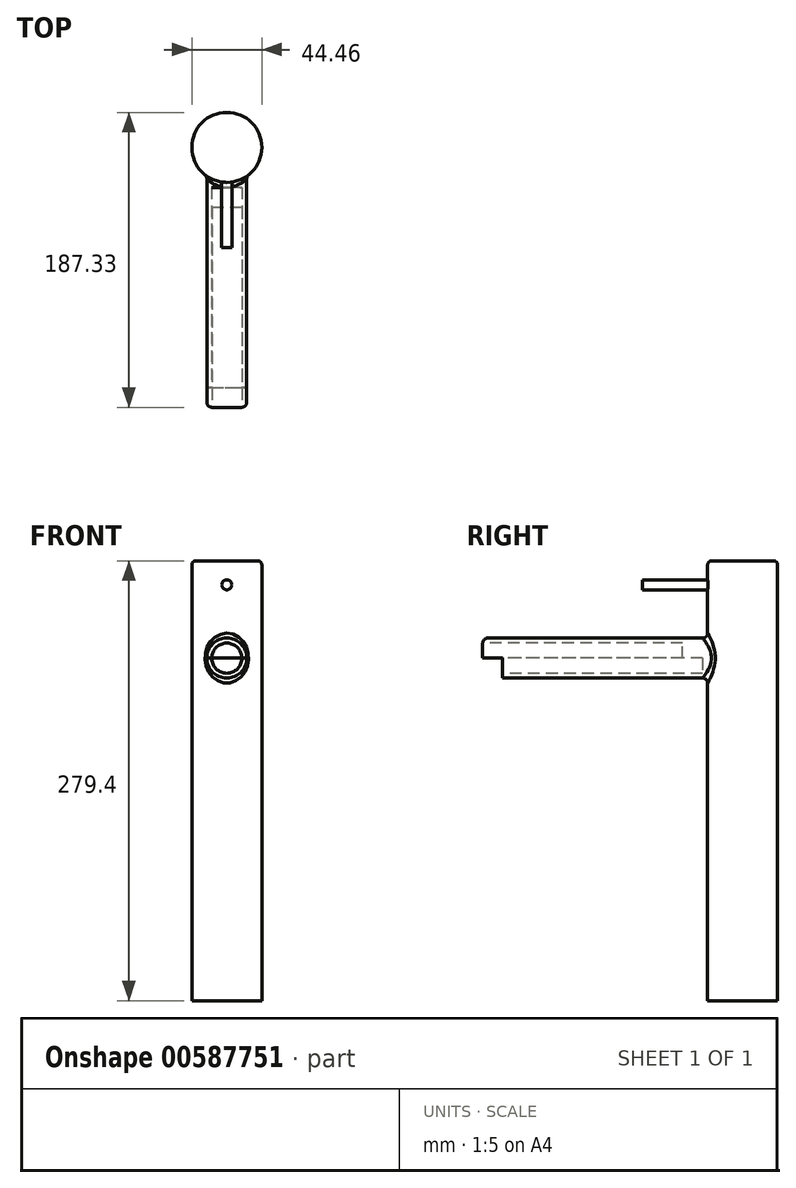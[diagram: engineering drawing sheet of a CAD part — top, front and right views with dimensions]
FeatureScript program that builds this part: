
annotation { "Feature Type Name" : "Feature", "Feature Type Description" : "" }
export const myFeature = defineFeature(function(context is Context, id is Id, definition is map)
    precondition{}
    {
        {
            var Q0;
            Q0=qCreatedBy(makeId("Top.planeOp"),FACE);
            var sketch = newSketch(context, id + "F0", { "sketchPlane" : qUnion([Q0])});
            skCircle(sketch, "E0", {"center": v(0, 0) * mm, "radius": 22.23 * mm});
            skSolve(sketch);
        }
        {
            var Q0;
            Q0=makeQuery(id+"F0.imprint","IMPRINT",FACE,{"disambiguationData":[TD([[makeQuery(id+"F0.imprint","IMPRINT",EDGE,{"derivedFrom":sQuery(id+"F0.wireOp",EDGE,"E0")}),1.0]])]});
            extrude(context, id + "F1", {"entities" : qUnion([Q0]), "depth" : 279.4 * mm, "offsetDistance" : 25.4 * mm});
        }
        {
            var Q0;
            Q0=makeQuery(id+"F1.opExtrude","CAP_EDGE",EDGE,{"disambiguationData":[OSD([sQuery(id+"F0.wireOp",EDGE,"E0")])],"isStart":false});
            fillet(context, id + "F2", {"entities" : qUnion([Q0]), "radius" : 2.54 * mm, "tangentPropagation" : true, "allowEdgeOverflow" : false});
        }
        {
            var Q0;
            Q0=qCreatedBy(makeId("Front.planeOp"),FACE);
            var sketch = newSketch(context, id + "F3", { "sketchPlane" : qUnion([Q0])});
            skCircle(sketch, "E1", {"center": v(0, 217.6) * mm, "radius": 12.7 * mm});
            skSolve(sketch);
        }
        {
            var Q0;
            Q0 = qSketchRegion(id + "F3", true);
            extrude(context, id + "F4", {"entities" : qUnion([Q0]), "operationType" : NewBodyOperationType.ADD, "depth" : 152.4 * mm, "offsetDistance" : 25.4 * mm});
        }
        {
            var Q0;
            Q0=makeQuery(id+"F4.boolean.opBoolean","INTERSECT",EDGE,{"derivedFrom":[makeQuery(id+"F1.opExtrude","SWEPT_FACE",FACE,{"disambiguationData":[OSD([sQuery(id+"F0.wireOp",EDGE,"E0")])]}),makeQuery(id+"F4.opExtrude","SWEPT_FACE",FACE,{"disambiguationData":[OSD([sQuery(id+"F3.wireOp",EDGE,"E1")])]})]});
            fillet(context, id + "F5", {"entities" : qUnion([Q0]), "radius" : 3.17 * mm, "tangentPropagation" : true, "allowEdgeOverflow" : false});
        }
        {
            var Q0;
            Q0=makeQuery(id+"F4.opExtrude","CAP_FACE",FACE,{"disambiguationData":[OSD([sQuery(id+"F3.wireOp",EDGE,"E1")])],"isStart":false});
            var sketch = newSketch(context, id + "F6", { "sketchPlane" : qUnion([Q0])});
            skLineSegment(sketch, "E2", {"start": v(0, 217.6) * mm, "end": v(12.7, 217.6) * mm});
            skLineSegment(sketch, "E3", {"start": v(0, 217.6) * mm, "end": v(-12.7, 217.6) * mm});
            skSolve(sketch);
        }
        {
            var Q0;
            {var subQ0=sQuery(id+"F6.wireOp",EDGE,"E2");Q0=makeQuery(id+"F6.imprint","IMPRINT",FACE,{"disambiguationData":[TD([[makeQuery(id+"F6.imprint","IMPRINT",EDGE,{"derivedFrom":subQ0}),1.0]])]});}
            extrude(context, id + "F7", {"entities" : qUnion([Q0]), "operationType" : NewBodyOperationType.ADD, "depth" : 12.7 * mm, "offsetDistance" : 25.4 * mm});
        }
        {
            var Q0;
            Q0=makeQuery(id+"F7.opExtrude","CAP_EDGE",EDGE,{"disambiguationData":[OSD([sQuery(id+"F3.wireOp",EDGE,"E1")])],"isStart":false});
            fillet(context, id + "F8", {"entities" : qUnion([Q0]), "radius" : 3.17 * mm, "tangentPropagation" : true, "allowEdgeOverflow" : false});
        }
        {
            var Q0;
            Q0=makeQuery(id+"F4.opExtrude","CAP_FACE",FACE,{"disambiguationData":[OSD([sQuery(id+"F3.wireOp",EDGE,"E1")])],"isStart":false});
            var sketch = newSketch(context, id + "F9", { "sketchPlane" : qUnion([Q0])});
            skCircle(sketch, "E4", {"center": v(0, 217.6) * mm, "radius": 9.6 * mm});
            skSolve(sketch);
        }
        {
            var Q0;
            {var subQ0=sQuery(id+"F9.wireOp",EDGE,"E4");var subQ1=makeQuery(id+"F7.opExtrude","CAP_EDGE",EDGE,{"disambiguationData":[OSD([sQuery(id+"F6.wireOp",EDGE,"E2"),sQuery(id+"F6.wireOp",EDGE,"E3")])],"isStart":true});var subQ2=makeQuery(id+"F9.imprint","INTERSECT",VERTEX,{"disambiguationData":[OD(0.0)],"derivedFrom":[subQ1,subQ0]});Q0=makeQuery(id+"F9.imprint","IMPRINT",FACE,{"disambiguationData":[TD([[makeQuery(id+"F9.imprint","IMPRINT",EDGE,{"disambiguationData":[TD([[subQ2,1.0]])],"derivedFrom":subQ0}),1.0]])]});}
            var Q1;
            Q1=makeQuery(id+"F7.opExtrude","CAP_FACE",FACE,{"disambiguationData":[OSD([sQuery(id+"F3.wireOp",EDGE,"E1"),sQuery(id+"F6.wireOp",EDGE,"E2"),sQuery(id+"F6.wireOp",EDGE,"E3")])],"isStart":false});
            extrude(context, id + "F10", {"entities" : qUnion([Q0, Q1]), "operationType" : NewBodyOperationType.REMOVE, "oppositeDirection" : true, "depth" : 127 * mm, "offsetDistance" : 25.4 * mm});
        }
        {
            var Q0;
            Q0=qCreatedBy(makeId("Front.planeOp"),FACE);
            var sketch = newSketch(context, id + "F11", { "sketchPlane" : qUnion([Q0])});
            skCircle(sketch, "E5", {"center": v(0, 264.16) * mm, "radius": 3.18 * mm});
            skSolve(sketch);
        }
        {
            var Q0;
            Q0 = qSketchRegion(id + "F11", true);
            extrude(context, id + "F12", {"entities" : qUnion([Q0]), "operationType" : NewBodyOperationType.ADD, "depth" : 63.5 * mm, "offsetDistance" : 25.4 * mm});
        }
    });
